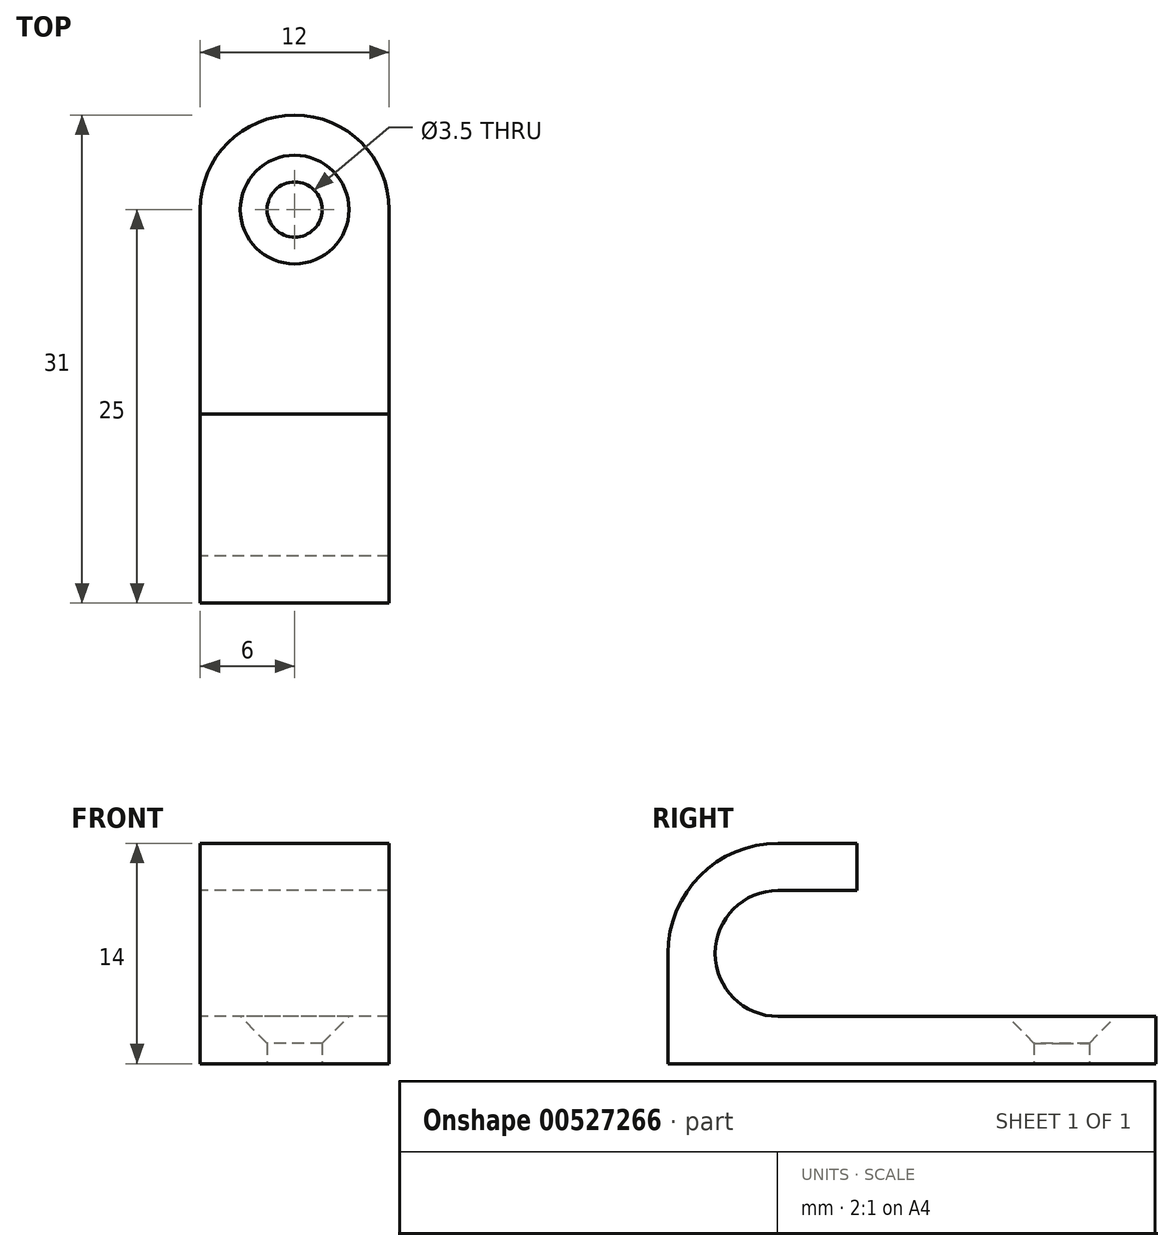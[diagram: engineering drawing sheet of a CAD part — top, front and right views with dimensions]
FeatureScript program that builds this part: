
annotation { "Feature Type Name" : "Feature", "Feature Type Description" : "" }
export const myFeature = defineFeature(function(context is Context, id is Id, definition is map)
    precondition{}
    {
        {
            var Q0;
            Q0=qCreatedBy(makeId("Top.planeOp"),FACE);
            var sketch = newSketch(context, id + "F0", { "sketchPlane" : qUnion([Q0])});
            skLineSegment(sketch, "E0.bottom", {"start": v(-6, 12.5) * mm, "end": v(6, 12.5) * mm});
            skLineSegment(sketch, "E0.top", {"start": v(-6, -12.5) * mm, "end": v(6, -12.5) * mm});
            skLineSegment(sketch, "E0.left", {"start": v(-6, 12.5) * mm, "end": v(-6, -12.5) * mm});
            skLineSegment(sketch, "E0.right", {"start": v(6, 12.5) * mm, "end": v(6, -12.5) * mm});
            skPoint(sketch, "E1", {"position": v(-6, 0) * mm});
            skPoint(sketch, "E2", {"position": v(0, 12.5) * mm});
            skCircle(sketch, "E3", {"center": v(0, 12.5) * mm, "radius": 6 * mm});
            skCircle(sketch, "E4", {"center": v(0, 12.5) * mm, "radius": 1.75 * mm});
            skSolve(sketch);
        }
        {
            var Q0;
            Q0=makeQuery(id+"F0.imprint","IMPRINT",FACE,{"disambiguationData":[TD([[makeQuery(id+"F0.imprint","IMPRINT",EDGE,{"derivedFrom":sQuery(id+"F0.wireOp",EDGE,"E0.top")}),1.0]])]});
            var Q1;
            {var subQ0=sQuery(id+"F0.wireOp",EDGE,"E3");var subQ1=sQuery(id+"F0.wireOp",EDGE,"E0.bottom");var subQ2=makeQuery(id+"F0.imprint","INTERSECT",VERTEX,{"disambiguationData":[OD(0.0)],"derivedFrom":[subQ1,subQ0]});Q1=makeQuery(id+"F0.imprint","IMPRINT",FACE,{"disambiguationData":[TD([[makeQuery(id+"F0.imprint","IMPRINT",EDGE,{"disambiguationData":[TD([[subQ2,-1.0]])],"derivedFrom":subQ1}),1.0]])]});}
            var Q2;
            {var subQ0=sQuery(id+"F0.wireOp",EDGE,"E3");var subQ1=sQuery(id+"F0.wireOp",EDGE,"E0.bottom");var subQ2=makeQuery(id+"F0.imprint","INTERSECT",VERTEX,{"disambiguationData":[OD(0.0)],"derivedFrom":[subQ1,subQ0]});Q2=makeQuery(id+"F0.imprint","IMPRINT",FACE,{"disambiguationData":[TD([[makeQuery(id+"F0.imprint","IMPRINT",EDGE,{"disambiguationData":[TD([[subQ2,-1.0]])],"derivedFrom":subQ1}),-1.0]])]});}
            extrude(context, id + "F1", {"entities" : qUnion([Q0, Q1, Q2]), "depth" : 3 * mm, "offsetDistance" : 25 * mm});
        }
        {
            var Q0;
            Q0=makeQuery(id+"F1.opExtrude","SWEPT_FACE",FACE,{"disambiguationData":[OSD([sQuery(id+"F0.wireOp",EDGE,"E0.left")])]});
            var sketch = newSketch(context, id + "F2", { "sketchPlane" : qUnion([Q0])});
            skArc(sketch, "E5", {"start": v(12.5, 7) * mm, "mid": v(10.45, 11.95) * mm, "end": v(5.5, 14) * mm});
            skArc(sketch, "E6", {"start": v(5.5, 3) * mm, "mid": v(9.5, 7) * mm, "end": v(5.5, 11) * mm});
            skLineSegment(sketch, "E7", {"start": v(12.5, 3) * mm, "end": v(12.5, 7) * mm});
            skLineSegment(sketch, "E8", {"start": v(12.5, 3) * mm, "end": v(5.5, 3) * mm});
            skLineSegment(sketch, "E9.bottom", {"start": v(5.5, 14) * mm, "end": v(0.5, 14) * mm});
            skLineSegment(sketch, "E9.top", {"start": v(5.5, 11) * mm, "end": v(0.5, 11) * mm});
            skLineSegment(sketch, "E9.right", {"start": v(0.5, 14) * mm, "end": v(0.5, 11) * mm});
            skSolve(sketch);
        }
        {
            var Q0;
            Q0=makeQuery(id+"F2.imprint","IMPRINT",FACE,{"disambiguationData":[TD([[makeQuery(id+"F2.imprint","IMPRINT",EDGE,{"derivedFrom":sQuery(id+"F2.wireOp",EDGE,"E5")}),1.0]])]});
            var Q1;
            Q1=makeQuery(id+"F1.opExtrude","SWEPT_FACE",FACE,{"disambiguationData":[OSD([sQuery(id+"F0.wireOp",EDGE,"E0.right")])]});
            extrude(context, id + "F3", {"entities" : qUnion([Q0]), "operationType" : NewBodyOperationType.ADD, "endBound" : BoundingType.UP_TO_SURFACE, "oppositeDirection" : true, "depth" : 25 * mm, "endBoundEntityFace" : qUnion([Q1]), "offsetDistance" : 25 * mm});
        }
        {
            var Q0;
            Q0=makeQuery(id+"F1.opExtrude","CAP_EDGE",EDGE,{"disambiguationData":[OSD([sQuery(id+"F0.wireOp",EDGE,"E4")])],"isStart":false});
            chamfer(context, id + "F4", {"entities" : qUnion([Q0]), "width" : 1.7 * mm, "tangentPropagation" : true});
        }
    });
